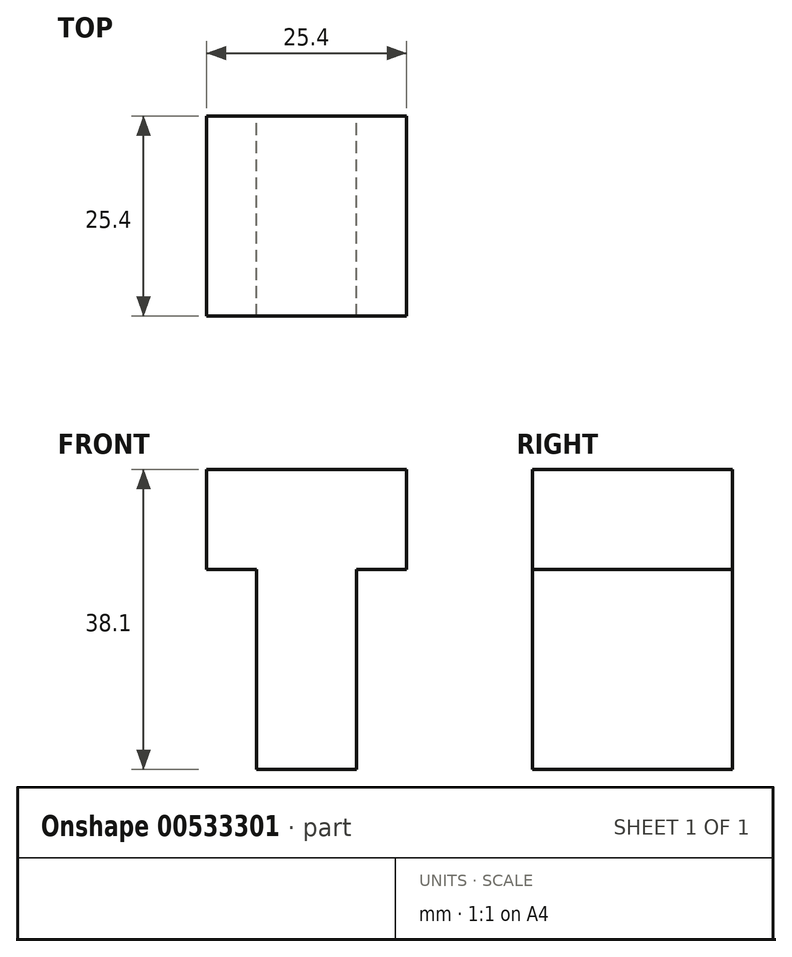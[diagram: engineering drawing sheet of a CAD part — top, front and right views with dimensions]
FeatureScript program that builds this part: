
annotation { "Feature Type Name" : "Feature", "Feature Type Description" : "" }
export const myFeature = defineFeature(function(context is Context, id is Id, definition is map)
    precondition{}
    {
        {
            var Q0;
            Q0=qCreatedBy(makeId("Front.planeOp"),FACE);
            var sketch = newSketch(context, id + "F0", { "sketchPlane" : qUnion([Q0])});
            skLineSegment(sketch, "E0", {"start": v(-24.95, 17.82) * mm, "end": v(-24.95, -7.58) * mm});
            skLineSegment(sketch, "E1", {"start": v(-24.95, -7.58) * mm, "end": v(-12.25, -7.58) * mm});
            skLineSegment(sketch, "E2", {"start": v(-12.25, -7.58) * mm, "end": v(-12.25, 17.82) * mm});
            skLineSegment(sketch, "E3", {"start": v(-12.25, 17.82) * mm, "end": v(-5.9, 17.82) * mm});
            skLineSegment(sketch, "E4", {"start": v(-5.9, 17.82) * mm, "end": v(-5.9, 30.52) * mm});
            skLineSegment(sketch, "E5", {"start": v(-5.9, 30.52) * mm, "end": v(-31.3, 30.52) * mm});
            skLineSegment(sketch, "E6", {"start": v(-31.3, 30.52) * mm, "end": v(-31.3, 17.82) * mm});
            skLineSegment(sketch, "E7", {"start": v(-31.3, 17.82) * mm, "end": v(-24.95, 17.82) * mm});
            skSolve(sketch);
        }
        {
            var Q0;
            Q0=qCreatedBy(makeId("Front.planeOp"),FACE);
            var sketch = newSketch(context, id + "F1", { "sketchPlane" : qUnion([Q0])});
            skSolve(sketch);
        }
        {
            var Q0;
            Q0 = qSketchRegion(id + "F1", true);
            var Q1;
            Q1=makeQuery(id+"F0.imprint","IMPRINT",FACE,{"disambiguationData":[TD([[makeQuery(id+"F0.imprint","IMPRINT",EDGE,{"derivedFrom":sQuery(id+"F0.wireOp",EDGE,"E0")}),1.0]])]});
            extrude(context, id + "F2", {"entities" : qUnion([Q0, Q1]), "depth" : 25.4 * mm, "offsetDistance" : 25.4 * mm});
        }
    });
